# Revit family: ROTADO_Вентилятор_Разгонный_РВО B
name_source: partatom
category: Оборудование
units: mm (PartAtom-declared; Revit-internal decimal feet)

## family parameters
Всегда вертикально = Да
Классификация = Нет
На основе рабочей плоскости = Нет
Общий = Нет
При загрузке вырезать с полостями = Нет
Размер круглого соединителя = Использовать диаметр
Тип детали = Нормальный
Точка расчета площади = Нет

## types (4) — shared parameters
ADSK_URL документации изделия = https://rotado.ru
ADSK_URL страницы изделия = https://rotado.ru
ADSK_Версия Revit = 2019
ADSK_Единица измерения = шт.
ADSK_Завод-изготовитель = ROTADO
ADSK_Классификация нагрузок = Прочее
ADSK_Количество = 1
ADSK_Количество фаз = 3
ADSK_Количество фаз числовое = 3
ADSK_Коэффициент мощности = 1
ADSK_Материал = ROTADO_Сталь_Нержавеющая_Оцинкованная
ADSK_Наименование = Разгонные вентиляторы с ременным приводом
ADSK_Напряжение = 380 В
URL = https://rotado.ru
Изготовитель = ROTADO
Логотип_Видимость = Да
Производитель_Контакты_Телефон = 88007002460

## per-type parameters (varying)
| type | A | ADSK_Марка | ADSK_Масса | ADSK_Масса_Текст | ADSK_Номинальная мощность | ADSK_Обозначение | ADSK_Полная мощность | ADSK_Размер_Высота | ADSK_Размер_Диаметр | ADSK_Размер_Длина | ADSK_Размер_Ширина | A_1 | D | G | k |
| Вентилятор_Разгонный_РВО(B)-1000-Combo430 | 1100 мм | РВО(B)-1000-Combo430 | 40 | 40 | 750 Вт | РВО(B)-1000-Combo430 | 750 В·А | 1100 мм | 1000 мм | 445 мм | 1100 мм | 1160 мм | 1000 мм | 445 мм | 12 мм |
| Вентилятор_Разгонный_РВО(B)-1100-Combo430 | 1220 мм | РВО(B)-1100-Combo430 | 49 | 49 кг | 750 Вт | РВО(B)-1100-Combo430 | 750 В·А | 1220 мм | 1100 мм | 445 мм | 1220 мм | 1280 мм | 1100 мм | 445 мм | 13 мм |
| Вентилятор_Разгонный_РВО(B)-1270-Combo430 | 1380 мм | РВО(B)-1270-Combo430 | 57 | 57 кг | 1500 Вт | РВО(B)-1270-Combo430 | 1500 В·А | 1380 мм | 1270 мм | 495 мм | 1380 мм | 1440 мм | 1270 мм | 495 мм | 15 мм |
| Вентилятор_Разгонный_РВО(B)-1400-Combo430 | 1530 мм | РВО(B)-1400-Combo430 | 62 | 62 кг | 1500 Вт | РВО(B)-1400-Combo430 | 1500 В·А | 1530 мм | 1400 мм | 495 мм | 1530 мм | 1590 мм | 1400 мм | 495 мм | 17 мм |
